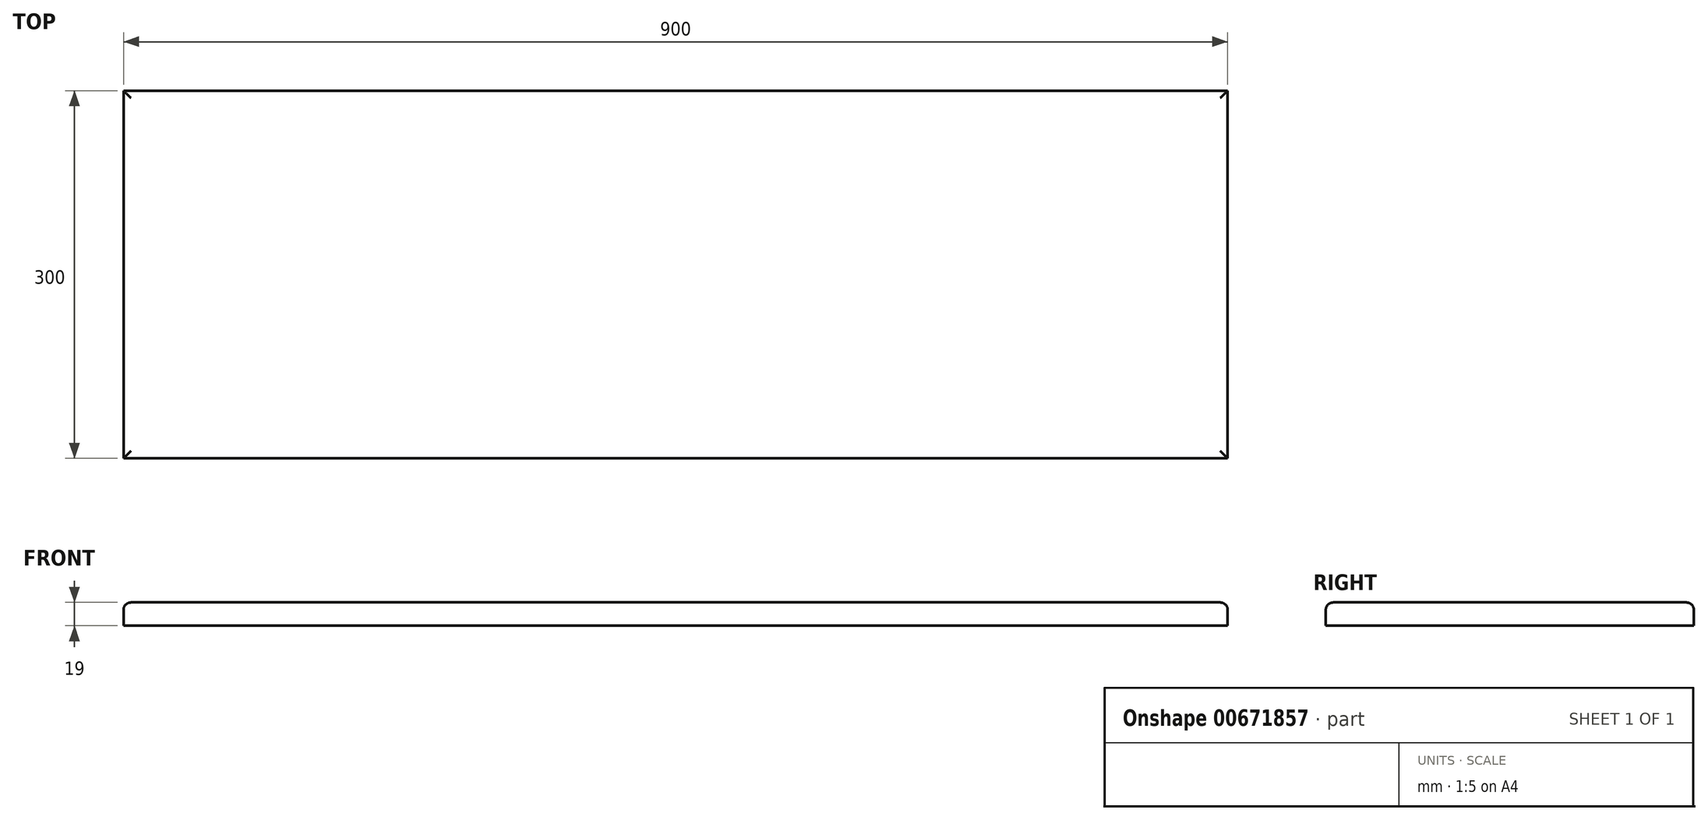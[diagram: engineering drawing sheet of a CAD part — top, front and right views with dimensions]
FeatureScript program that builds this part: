
annotation { "Feature Type Name" : "Feature", "Feature Type Description" : "" }
export const myFeature = defineFeature(function(context is Context, id is Id, definition is map)
    precondition{}
    {
        {
            var Q0;
            Q0=qCreatedBy(makeId("Top.planeOp"),FACE);
            var sketch = newSketch(context, id + "F0", { "sketchPlane" : qUnion([Q0])});
            skLineSegment(sketch, "E0.bottom", {"start": v(-450, -150) * mm, "end": v(450, -150) * mm});
            skLineSegment(sketch, "E0.top", {"start": v(-450, 150) * mm, "end": v(450, 150) * mm});
            skLineSegment(sketch, "E0.left", {"start": v(-450, -150) * mm, "end": v(-450, 150) * mm});
            skLineSegment(sketch, "E0.right", {"start": v(450, -150) * mm, "end": v(450, 150) * mm});
            skPoint(sketch, "E0.middle", {"position": v(0, 0) * mm});
            skSolve(sketch);
        }
        {
            var Q0;
            Q0=makeQuery(id+"F0.imprint","IMPRINT",FACE,{"disambiguationData":[TD([[makeQuery(id+"F0.imprint","IMPRINT",EDGE,{"derivedFrom":sQuery(id+"F0.wireOp",EDGE,"E0.bottom")}),1.0]])]});
            extrude(context, id + "F1", {"entities" : qUnion([Q0]), "depth" : 19 * mm, "offsetDistance" : 25 * mm});
        }
        {
            var Q0;
            Q0=makeQuery(id+"F1.opExtrude","CAP_EDGE",EDGE,{"disambiguationData":[OSD([sQuery(id+"F0.wireOp",EDGE,"E0.left")])],"isStart":false});
            var Q1;
            Q1=makeQuery(id+"F1.opExtrude","CAP_EDGE",EDGE,{"disambiguationData":[OSD([sQuery(id+"F0.wireOp",EDGE,"E0.top")])],"isStart":false});
            var Q2;
            Q2=makeQuery(id+"F1.opExtrude","CAP_EDGE",EDGE,{"disambiguationData":[OSD([sQuery(id+"F0.wireOp",EDGE,"E0.right")])],"isStart":false});
            var Q3;
            Q3=makeQuery(id+"F1.opExtrude","CAP_EDGE",EDGE,{"disambiguationData":[OSD([sQuery(id+"F0.wireOp",EDGE,"E0.bottom")])],"isStart":false});
            fillet(context, id + "F2", {"entities" : qUnion([Q0, Q1, Q2, Q3]), "radius" : 6 * mm, "tangentPropagation" : true, "allowEdgeOverflow" : false});
        }
    });
